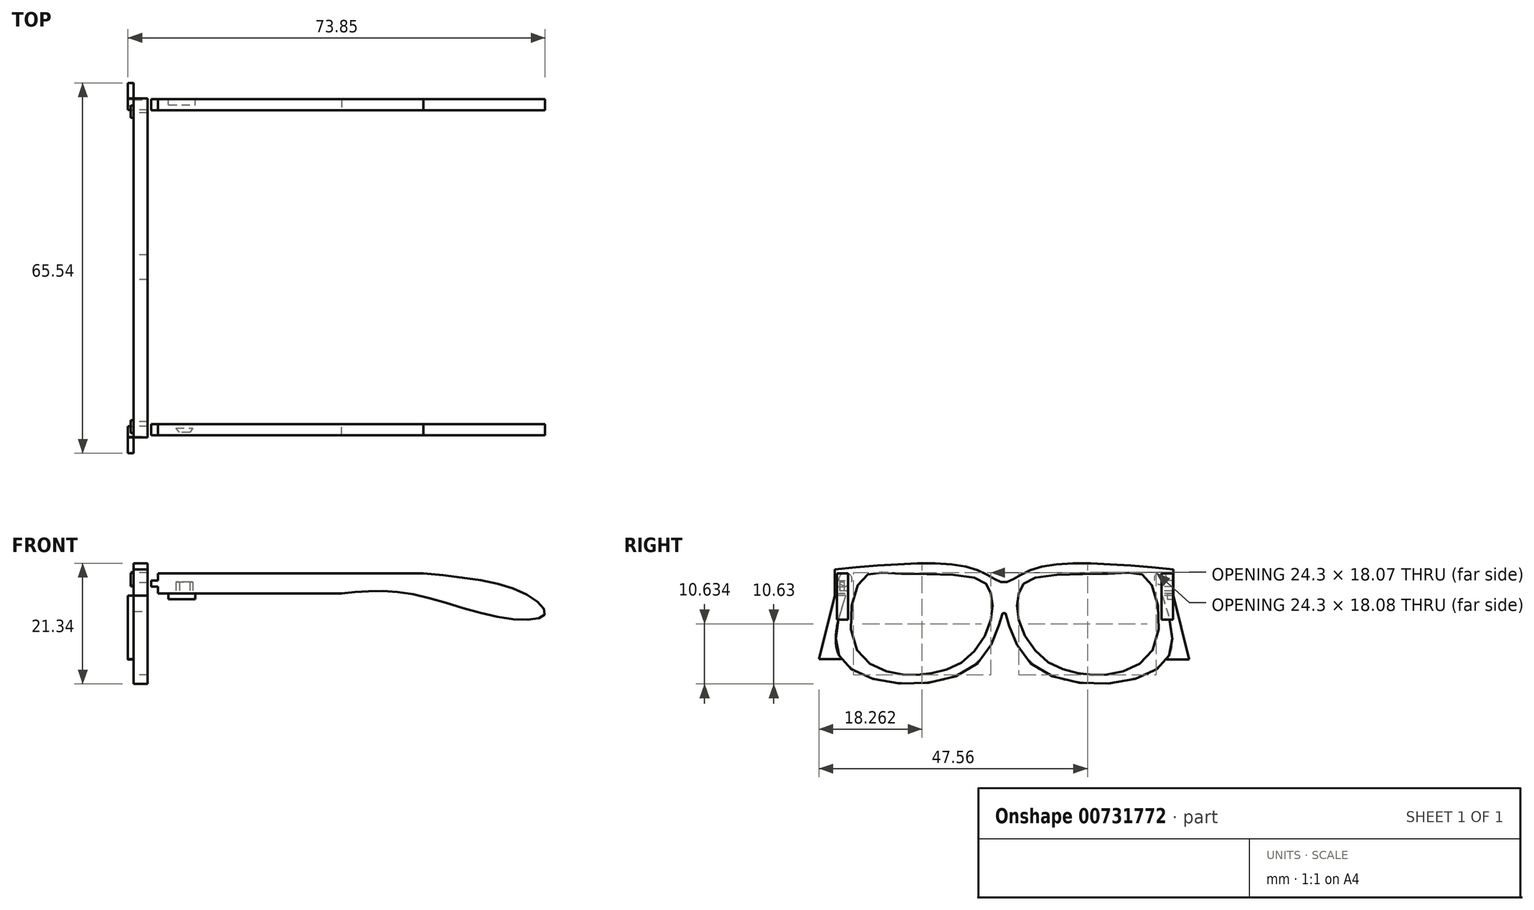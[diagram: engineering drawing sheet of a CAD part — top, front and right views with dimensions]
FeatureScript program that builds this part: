
annotation { "Feature Type Name" : "Feature", "Feature Type Description" : "" }
export const myFeature = defineFeature(function(context is Context, id is Id, definition is map)
    precondition{}
    {
        {
            var Q0;
            Q0=qCreatedBy(makeId("Front.planeOp"),FACE);
            var sketch = newSketch(context, id + "F0", { "sketchPlane" : qUnion([Q0])});
            skLineSegment(sketch, "E0", {"start": v(-30.17, 0) * mm, "end": v(-30.17, 1.2) * mm});
            skLineSegment(sketch, "E1", {"start": v(-30.17, 1.2) * mm, "end": v(-31.35, 1.2) * mm});
            skLineSegment(sketch, "E2", {"start": v(-31.35, 1.2) * mm, "end": v(-31.35, 2.3) * mm});
            skLineSegment(sketch, "E3", {"start": v(-31.35, 2.3) * mm, "end": v(-30.17, 2.3) * mm});
            skLineSegment(sketch, "E4", {"start": v(-30.17, 2.3) * mm, "end": v(-30.17, 3.57) * mm});
            skLineSegment(sketch, "E5", {"start": v(-30.17, 3.57) * mm, "end": v(16.84, 3.57) * mm});
            skLineSegment(sketch, "E6", {"start": v(-30.17, 0) * mm, "end": v(2.32, 0) * mm});
            skFitSpline(sketch, "E7", {"points": [v(16.84, 3.57) * mm, v(34.72, 0) * mm, v(38.32, -3.7) * mm, v(31, -4.33) * mm, v(14.06, 0) * mm, v(2.32, 0) * mm], "startDerivative": vector(80.04, -8.07) * mm, "endDerivative": vector(-54.78, -5.44) * mm});
            skSolve(sketch);
        }
        {
            var Q0;
            Q0=makeQuery(id+"F0.imprint","IMPRINT",FACE,{"disambiguationData":[TD([[makeQuery(id+"F0.imprint","IMPRINT",EDGE,{"derivedFrom":sQuery(id+"F0.wireOp",EDGE,"E0")}),-1.0]])]});
            extrude(context, id + "F1", {"entities" : qUnion([Q0]), "endBound" : BoundingType.SYMMETRIC, "depth" : 2 * mm});
        }
        {
            var Q0;
            Q0=makeQuery(id+"F1.opExtrude","SWEPT_BODY",BODY,{"disambiguationData":[OSD([sQuery(id+"F0.wireOp",EDGE,"E0"),sQuery(id+"F0.wireOp",EDGE,"E1"),sQuery(id+"F0.wireOp",EDGE,"E2"),sQuery(id+"F0.wireOp",EDGE,"E3"),sQuery(id+"F0.wireOp",EDGE,"E4"),sQuery(id+"F0.wireOp",EDGE,"E5"),sQuery(id+"F0.wireOp",EDGE,"E6"),sQuery(id+"F0.wireOp",EDGE,"E7")])]});
            var Q1;
            Q1=makeQuery(id+"F1.opExtrude","CAP_FACE",FACE,{"disambiguationData":[OSD([sQuery(id+"F0.wireOp",EDGE,"E0"),sQuery(id+"F0.wireOp",EDGE,"E1"),sQuery(id+"F0.wireOp",EDGE,"E2"),sQuery(id+"F0.wireOp",EDGE,"E3"),sQuery(id+"F0.wireOp",EDGE,"E4"),sQuery(id+"F0.wireOp",EDGE,"E5"),sQuery(id+"F0.wireOp",EDGE,"E6"),sQuery(id+"F0.wireOp",EDGE,"E7")])],"isStart":false});
            mirror(context, id + "F2", {"entities" : qUnion([Q0]), "mirrorPlane" : qUnion([Q1])});
        }
        {
            var Q0;
            Q0=makeQuery(id+"F2.opPattern","COPY",BODY,{"derivedFrom":makeQuery(id+"F1.opExtrude","SWEPT_BODY",BODY,{"disambiguationData":[OSD([sQuery(id+"F0.wireOp",EDGE,"E0"),sQuery(id+"F0.wireOp",EDGE,"E1"),sQuery(id+"F0.wireOp",EDGE,"E2"),sQuery(id+"F0.wireOp",EDGE,"E3"),sQuery(id+"F0.wireOp",EDGE,"E4"),sQuery(id+"F0.wireOp",EDGE,"E5"),sQuery(id+"F0.wireOp",EDGE,"E6"),sQuery(id+"F0.wireOp",EDGE,"E7")])]}),"instanceName":"1"});
            transform(context, id + "F3", {"entities" : qUnion([Q0]), "transformType" : TransformType.TRANSLATION_3D, "dx" : 0 * mm, "dy" : 50.13 * mm, "dz" : 0 * mm, "makeCopy" : false});
        }
        {
            var Q0;
            Q0=qCreatedBy(makeId("Right.planeOp"),FACE);
            var sketch = newSketch(context, id + "F4", { "sketchPlane" : qUnion([Q0])});
            skLineSegment(sketch, "E8", {"start": v(53.4, 28.28) * mm, "end": v(53.4, 23.62) * mm});
            skLineSegment(sketch, "E9", {"start": v(-6.6, 23.62) * mm, "end": v(-6.6, 28.28) * mm});
            skPoint(sketch, "E10", {"position": v(28.4, 28.28) * mm});
            skPoint(sketch, "E11", {"position": v(18.4, 28.28) * mm});
            skPoint(sketch, "E12.2.internal.snap0", {"position": v(53.4, 25.95) * mm});
            skFitSpline(sketch, "E12", {"points": [v(53.4, 28.28) * mm, v(28.4, 28.28) * mm, v(23.4, 25.95) * mm, v(18.4, 28.28) * mm, v(-6.6, 28.28) * mm], "startDerivative": vector(-87.84, 8.09) * mm, "endDerivative": vector(-87.84, -8.09) * mm});
            skPoint(sketch, "E13", {"position": v(51.4, 23.62) * mm});
            skPoint(sketch, "E14", {"position": v(-4.6, 23.62) * mm});
            skFitSpline(sketch, "E15", {"points": [v(51.4, 23.62) * mm, v(51.4, 11.38) * mm, v(28.4, 11.38) * mm, v(23.4, 20.85) * mm, v(18.4, 11.38) * mm, v(-4.6, 11.38) * mm, v(-4.6, 23.62) * mm], "startDerivative": vector(30.78, -92.04) * mm, "endDerivative": vector(30.78, 92.04) * mm});
            skLineSegment(sketch, "E16", {"start": v(53.4, 23.62) * mm, "end": v(51.4, 23.62) * mm});
            skLineSegment(sketch, "E17", {"start": v(-4.6, 23.62) * mm, "end": v(-6.6, 23.62) * mm});
            skSolve(sketch);
        }
        {
            var Q0;
            Q0=makeQuery(id+"F4.imprint","IMPRINT",FACE,{"disambiguationData":[TD([[makeQuery(id+"F4.imprint","IMPRINT",EDGE,{"derivedFrom":sQuery(id+"F4.wireOp",EDGE,"E8")}),-1.0]])]});
            extrude(context, id + "F5", {"entities" : qUnion([Q0]), "endBound" : BoundingType.SYMMETRIC, "depth" : 2.5 * mm});
        }
        {
            var Q0;
            Q0=makeQuery(id+"F5.opExtrude","SWEPT_BODY",BODY,{"disambiguationData":[OSD([sQuery(id+"F4.wireOp",EDGE,"E8"),sQuery(id+"F4.wireOp",EDGE,"E9"),sQuery(id+"F4.wireOp",EDGE,"E12"),sQuery(id+"F4.wireOp",EDGE,"E15"),sQuery(id+"F4.wireOp",EDGE,"E16"),sQuery(id+"F4.wireOp",EDGE,"E17")])]});
            transform(context, id + "F6", {"entities" : qUnion([Q0]), "transformType" : TransformType.TRANSLATION_3D, "dx" : -33.23 * mm, "dy" : -4.17 * mm, "dz" : -24.03 * mm, "makeCopy" : false});
        }
        {
            var Q0;
            Q0=makeQuery(id+"F1.opExtrude","SWEPT_BODY",BODY,{"disambiguationData":[OSD([sQuery(id+"F0.wireOp",EDGE,"E0"),sQuery(id+"F0.wireOp",EDGE,"E1"),sQuery(id+"F0.wireOp",EDGE,"E2"),sQuery(id+"F0.wireOp",EDGE,"E3"),sQuery(id+"F0.wireOp",EDGE,"E4"),sQuery(id+"F0.wireOp",EDGE,"E5"),sQuery(id+"F0.wireOp",EDGE,"E6"),sQuery(id+"F0.wireOp",EDGE,"E7")])]});
            transform(context, id + "F7", {"entities" : qUnion([Q0]), "transformType" : TransformType.TRANSLATION_3D, "dx" : 0 * mm, "dy" : -9.4 * mm, "dz" : 0 * mm, "makeCopy" : false});
        }
        {
            var Q0;
            Q0=qCreatedBy(makeId("Right.planeOp"),FACE);
            var sketch = newSketch(context, id + "F8", { "sketchPlane" : qUnion([Q0])});
            skPoint(sketch, "E18", {"position": v(19.36, -3.2) * mm});
            skPoint(sketch, "E19", {"position": v(19.23, 1.99) * mm});
            skPoint(sketch, "E20", {"position": v(19.36, 0) * mm});
            skPoint(sketch, "E21", {"position": v(16.86, 0) * mm});
            skPoint(sketch, "E22", {"position": v(21.86, 0) * mm});
            skPoint(sketch, "E23", {"position": v(16.86, -4.94) * mm});
            skPoint(sketch, "E24", {"position": v(21.86, -4.94) * mm});
            skPoint(sketch, "E25", {"position": v(14.86, 0) * mm});
            skPoint(sketch, "E26", {"position": v(23.86, 0) * mm});
            skPoint(sketch, "E27", {"position": v(14.86, 2.49) * mm});
            skPoint(sketch, "E28", {"position": v(23.86, 2.49) * mm});
            skPoint(sketch, "E29", {"position": v(0, 2.49) * mm});
            skPoint(sketch, "E30", {"position": v(38.72, 2.49) * mm});
            skPoint(sketch, "E31", {"position": v(-6, 2.49) * mm});
            skPoint(sketch, "E32", {"position": v(44.72, 2.49) * mm});
            skPoint(sketch, "E33", {"position": v(-7.14, -4.94) * mm});
            skPoint(sketch, "E34", {"position": v(45.86, -4.94) * mm});
            skPoint(sketch, "E35", {"position": v(-7.14, -9.44) * mm});
            skPoint(sketch, "E36", {"position": v(45.86, -9.44) * mm});
            skPoint(sketch, "E37", {"position": v(0, -14.17) * mm});
            skPoint(sketch, "E38", {"position": v(38.72, -14.17) * mm});
            skPoint(sketch, "E39", {"position": v(6, -14.17) * mm});
            skPoint(sketch, "E40", {"position": v(32.72, -14.17) * mm});
            skPoint(sketch, "E41", {"position": v(12.26, -11.85) * mm});
            skPoint(sketch, "E42", {"position": v(12.26, 0) * mm});
            skPoint(sketch, "E43", {"position": v(26.46, 0) * mm});
            skPoint(sketch, "E44", {"position": v(-6, 3.53) * mm});
            skPoint(sketch, "E45", {"position": v(-5.94, 3.53) * mm});
            skPoint(sketch, "E46", {"position": v(0, 3.53) * mm});
            skFitSpline(sketch, "E47", {"points": [v(16.86, -0.02) * mm, v(14.86, 2.49) * mm, v(0, 3.53) * mm, v(-6, 2.49) * mm, v(-7.14, -9.44) * mm, v(0, -14.17) * mm, v(6, -14.17) * mm, v(12.26, -11.85) * mm, v(16.86, -4.94) * mm, v(16.86, -0.02) * mm]});
            skPoint(sketch, "E48", {"position": v(12.26, -11.76) * mm});
            skPoint(sketch, "E49", {"position": v(38.72, 3.53) * mm});
            skPoint(sketch, "E50", {"position": v(26.46, -11.76) * mm});
            skFitSpline(sketch, "E51", {"points": [v(21.86, 0) * mm, v(23.86, 2.49) * mm, v(38.72, 3.53) * mm, v(44.72, 2.49) * mm, v(45.86, -9.44) * mm, v(38.72, -14.17) * mm, v(32.72, -14.17) * mm, v(26.46, -11.76) * mm, v(21.86, -4.94) * mm, v(21.86, 0) * mm]});
            skPoint(sketch, "E52", {"position": v(18.84, -4.06) * mm});
            skPoint(sketch, "E53", {"position": v(19.62, -4.06) * mm});
            skSolve(sketch);
        }
        {
            var Q0;
            Q0=makeQuery(id+"F8.imprint","IMPRINT",FACE,{"disambiguationData":[TD([[makeQuery(id+"F8.imprint","IMPRINT",EDGE,{"derivedFrom":sQuery(id+"F8.wireOp",EDGE,"E47")}),1.0]])]});
            var Q1;
            Q1=makeQuery(id+"F8.imprint","IMPRINT",FACE,{"disambiguationData":[TD([[makeQuery(id+"F8.imprint","IMPRINT",EDGE,{"derivedFrom":sQuery(id+"F8.wireOp",EDGE,"E51")}),-1.0]])]});
            extrude(context, id + "F9", {"entities" : qUnion([Q0, Q1]), "operationType" : NewBodyOperationType.REMOVE, "oppositeDirection" : true, "depth" : 72.6 * mm});
        }
        {
            var Q0;
            Q0=makeQuery(id+"F5.opExtrude","CAP_FACE",FACE,{"disambiguationData":[OSD([sQuery(id+"F4.wireOp",EDGE,"E8"),sQuery(id+"F4.wireOp",EDGE,"E9"),sQuery(id+"F4.wireOp",EDGE,"E12"),sQuery(id+"F4.wireOp",EDGE,"E15"),sQuery(id+"F4.wireOp",EDGE,"E16"),sQuery(id+"F4.wireOp",EDGE,"E17")])],"isStart":true});
            var sketch = newSketch(context, id + "F10", { "sketchPlane" : qUnion([Q0])});
            skLineSegment(sketch, "E54", {"start": v(10.78, -0.41) * mm, "end": v(13.55, -11.67) * mm});
            skLineSegment(sketch, "E55", {"start": v(-49.22, -0.41) * mm, "end": v(-51.99, -11.73) * mm});
            skLineSegment(sketch, "E56", {"start": v(-51.99, -11.73) * mm, "end": v(-48.01, -11.73) * mm});
            skLineSegment(sketch, "E57", {"start": v(9.6, -11.66) * mm, "end": v(-48.06, -11.66) * mm, "construction": true});
            skLineSegment(sketch, "E58", {"start": v(13.55, -11.67) * mm, "end": v(9.6, -11.66) * mm});
            skSolve(sketch);
        }
        {
            var Q0;
            Q0=qSketchRegion(id+"F10",true);
            var Q1;
            Q1=makeQuery(id+"F10.imprint","IMPRINT",FACE,{"disambiguationData":[TD([[makeQuery(id+"F10.imprint","IMPRINT",EDGE,{"derivedFrom":sQuery(id+"F10.wireOp",EDGE,"E55")}),1.0]])]});
            var Q2;
            Q2=makeQuery(id+"F10.imprint","IMPRINT",FACE,{"disambiguationData":[TD([[makeQuery(id+"F10.imprint","IMPRINT",EDGE,{"derivedFrom":sQuery(id+"F10.wireOp",EDGE,"E54")}),-1.0]])]});
            extrude(context, id + "F11", {"entities" : qUnion([Q0, Q1, Q2]), "depth" : 1 * mm});
        }
        {
            var Q0;
            Q0=makeQuery(id+"F5.opExtrude","CAP_FACE",FACE,{"disambiguationData":[OSD([sQuery(id+"F4.wireOp",EDGE,"E8"),sQuery(id+"F4.wireOp",EDGE,"E9"),sQuery(id+"F4.wireOp",EDGE,"E12"),sQuery(id+"F4.wireOp",EDGE,"E15"),sQuery(id+"F4.wireOp",EDGE,"E16"),sQuery(id+"F4.wireOp",EDGE,"E17")])],"isStart":true});
            var sketch = newSketch(context, id + "F12", { "sketchPlane" : qUnion([Q0])});
            skCircle(sketch, "E59", {"center": v(8.85, 2.45) * mm, "radius": 1.17 * mm});
            skCircle(sketch, "E60", {"center": v(-46.9, 2.66) * mm, "radius": 1.09 * mm});
            skSolve(sketch);
        }
        {
            var Q0;
            Q0=qSketchRegion(id+"F12",true);
            extrude(context, id + "F13", {"entities" : qUnion([Q0]), "depth" : .5 * mm});
        }
        {
            var Q0;
            Q0=makeQuery(id+"F2.opPattern","COPY",FACE,{"derivedFrom":makeQuery(id+"F1.opExtrude","CAP_FACE",FACE,{"disambiguationData":[OSD([sQuery(id+"F0.wireOp",EDGE,"E0"),sQuery(id+"F0.wireOp",EDGE,"E1"),sQuery(id+"F0.wireOp",EDGE,"E2"),sQuery(id+"F0.wireOp",EDGE,"E3"),sQuery(id+"F0.wireOp",EDGE,"E4"),sQuery(id+"F0.wireOp",EDGE,"E5"),sQuery(id+"F0.wireOp",EDGE,"E6"),sQuery(id+"F0.wireOp",EDGE,"E7")])],"isStart":false}),"instanceName":"1"});
            var sketch = newSketch(context, id + "F14", { "sketchPlane" : qUnion([Q0])});
            skLineSegment(sketch, "E61.bottom", {"start": v(23.58, 3.57) * mm, "end": v(28.3, 3.57) * mm});
            skLineSegment(sketch, "E61.top", {"start": v(23.58, -1.02) * mm, "end": v(28.3, -1.02) * mm});
            skLineSegment(sketch, "E61.left", {"start": v(23.58, 3.57) * mm, "end": v(23.58, -1.02) * mm});
            skLineSegment(sketch, "E61.right", {"start": v(28.3, 3.57) * mm, "end": v(28.3, -1.02) * mm});
            skSolve(sketch);
        }
        {
            var Q0;
            {var subQ0=sQuery(id+"F14.wireOp",EDGE,"E61.top");Q0=makeQuery(id+"F14.imprint","IMPRINT",FACE,{"disambiguationData":[TD([[makeQuery(id+"F14.imprint","IMPRINT",EDGE,{"derivedFrom":subQ0}),1.0]])]});}
            extrude(context, id + "F15", {"entities" : qUnion([Q0]), "operationType" : NewBodyOperationType.ADD, "oppositeDirection" : true, "depth" : 1 * mm});
        }
        {
            var Q0;
            Q0=makeQuery(id+"F1.opExtrude","SWEPT_FACE",FACE,{"disambiguationData":[OSD([sQuery(id+"F0.wireOp",EDGE,"E6")])]});
            var sketch = newSketch(context, id + "F16", { "sketchPlane" : qUnion([Q0])});
            skLineSegment(sketch, "E62", {"start": v(-26.37, 9.9) * mm, "end": v(-27.01, 9.11) * mm});
            skLineSegment(sketch, "E63", {"start": v(-27.01, 9.11) * mm, "end": v(-24.03, 9.11) * mm});
            skLineSegment(sketch, "E64", {"start": v(-24.03, 9.11) * mm, "end": v(-24.5, 9.85) * mm});
            skLineSegment(sketch, "E65", {"start": v(-24.5, 9.85) * mm, "end": v(-26.37, 9.9) * mm});
            skSolve(sketch);
        }
        {
            var Q0;
            Q0=qSketchRegion(id+"F16",true);
            extrude(context, id + "F17", {"entities" : qUnion([Q0]), "operationType" : NewBodyOperationType.REMOVE, "oppositeDirection" : true, "depth" : 2 * mm});
        }
    });
